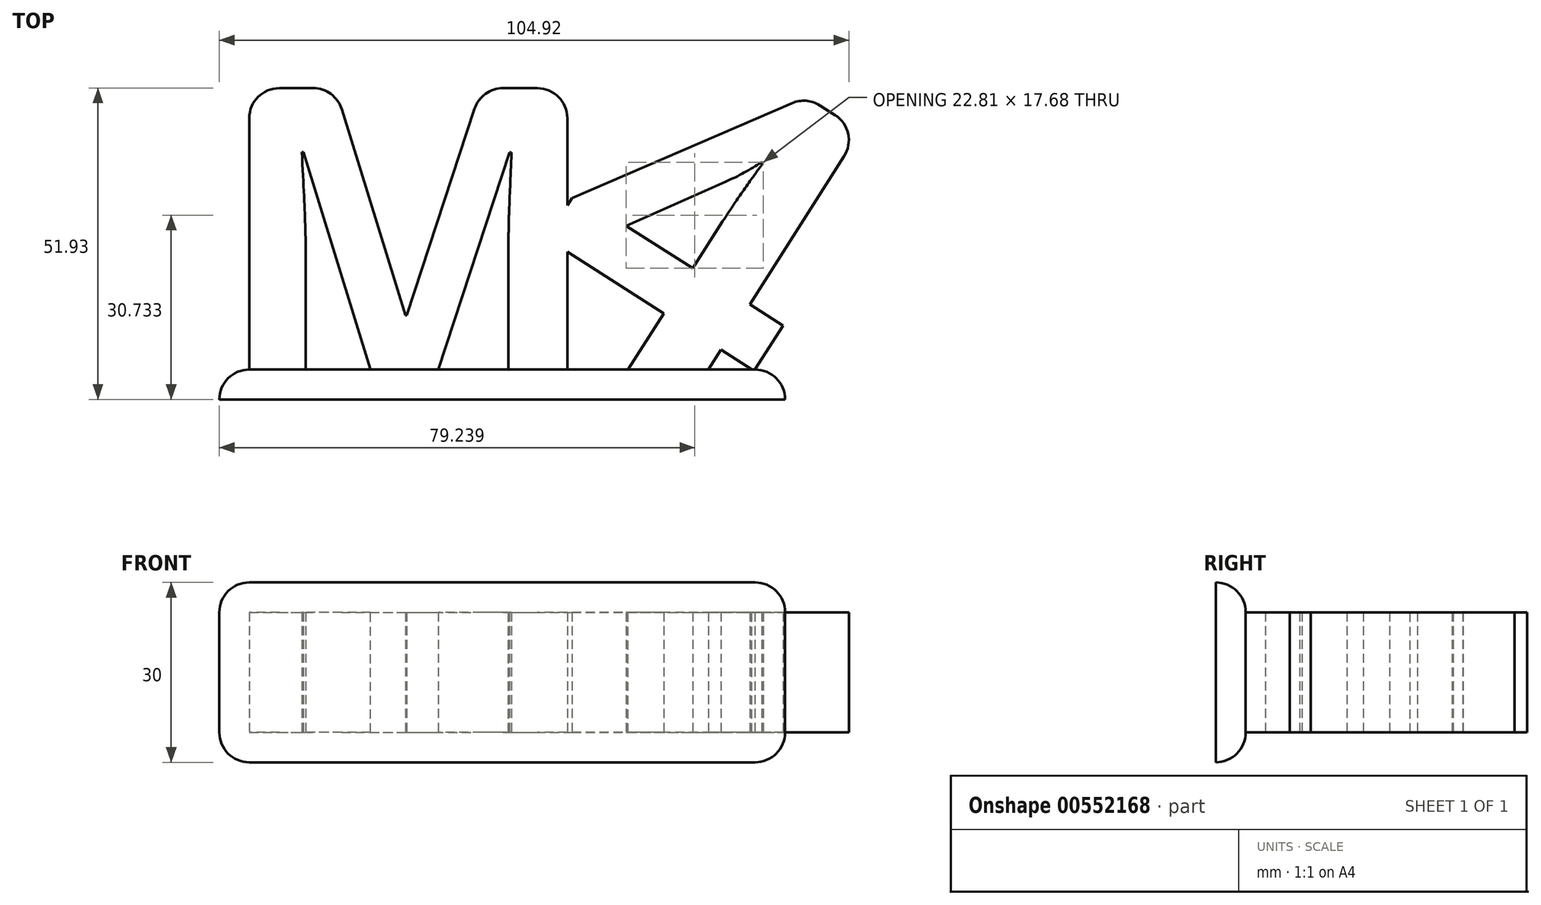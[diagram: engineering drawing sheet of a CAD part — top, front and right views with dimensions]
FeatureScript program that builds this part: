
annotation { "Feature Type Name" : "Feature", "Feature Type Description" : "" }
export const myFeature = defineFeature(function(context is Context, id is Id, definition is map)
    precondition{}
    {
        {
            var Q0;
            Q0=qCreatedBy(makeId("Top.planeOp"),FACE);
            var sketch = newSketch(context, id + "F0", { "sketchPlane" : qUnion([Q0])});
            skText(sketch, "E0", { "text": "M", "fontName": "OpenSans-Bold.ttf"});
            const initialGuessF0  = {"E0": [-0.04888, -0.02717, 1, 0, 0.05]};
            skSetInitialGuess(sketch, initialGuessF0);
            skSolve(sketch);
        }
        {
            var Q0;
            Q0=makeQuery(id+"F0.imprint","IMPRINT",FACE,{"disambiguationData":[TD([[makeQuery(id+"F0.imprint","IMPRINT",EDGE,{"derivedFrom":sQuery(id+"F0.wireOp",EDGE,"E0.sketch_text.stroke-0")}),-1.0]])]});
            extrude(context, id + "F1", {"entities" : qUnion([Q0]), "depth" : 20 * mm, "offsetDistance" : 25.4 * mm});
        }
        {
            var Q0;
            Q0=qCreatedBy(makeId("Top.planeOp"),FACE);
            var sketch = newSketch(context, id + "F2", { "sketchPlane" : qUnion([Q0])});
            skText(sketch, "E1", { "text": "4", "fontName": "OpenSans-Bold.ttf"});
            const initialGuessF2  = {"E1": [-0.00034, -0.01151, 0.8435, -0.53714, 0.055]};
            skSetInitialGuess(sketch, initialGuessF2);
            skSolve(sketch);
        }
        {
            var Q0;
            Q0=makeQuery(id+"F2.imprint","IMPRINT",FACE,{"disambiguationData":[TD([[makeQuery(id+"F2.imprint","IMPRINT",EDGE,{"derivedFrom":sQuery(id+"F2.wireOp",EDGE,"E1.sketch_text.stroke-0")}),-1.0]])]});
            var sketch = newSketch(context, id + "F3", { "sketchPlane" : qUnion([Q0])});
            skLineSegment(sketch, "E2", {"start": v(-47.64, -24.52) * mm, "end": v(-47.64, -29.52) * mm});
            skLineSegment(sketch, "E3", {"start": v(46.66, -24.52) * mm, "end": v(46.66, -29.52) * mm});
            skLineSegment(sketch, "E4", {"start": v(46.66, -29.52) * mm, "end": v(-47.64, -29.52) * mm});
            skLineSegment(sketch, "E5", {"start": v(46.66, -24.52) * mm, "end": v(-47.64, -24.52) * mm});
            skSolve(sketch);
        }
        {
            var Q0;
            Q0=makeQuery(id+"F2.imprint","IMPRINT",FACE,{"disambiguationData":[TD([[makeQuery(id+"F2.imprint","IMPRINT",EDGE,{"derivedFrom":sQuery(id+"F2.wireOp",EDGE,"E1.sketch_text.stroke-0")}),-1.0]])]});
            extrude(context, id + "F4", {"entities" : qUnion([Q0]), "operationType" : NewBodyOperationType.ADD, "depth" : 20 * mm, "offsetDistance" : 25 * mm});
        }
        {
            var Q0;
            Q0=makeQuery(id+"F1.opExtrude","SWEPT_EDGE",EDGE,{"disambiguationData":[OSD([sQuery(id+"F0.wireOp",EDGE,"E0.sketch_text.stroke-5"),sQuery(id+"F0.wireOp",EDGE,"E0.sketch_text.stroke-6")])]});
            fillet(context, id + "F5", {"entities" : qUnion([Q0]), "radius" : 5 * mm, "tangentPropagation" : true, "allowEdgeOverflow" : false});
        }
        {
            var Q0;
            Q0=makeQuery(id+"F1.opExtrude","SWEPT_EDGE",EDGE,{"disambiguationData":[OSD([sQuery(id+"F0.wireOp",EDGE,"E0.sketch_text.stroke-6"),sQuery(id+"F0.wireOp",EDGE,"E0.sketch_text.stroke-7")])]});
            fillet(context, id + "F6", {"entities" : qUnion([Q0]), "radius" : 5 * mm, "tangentPropagation" : true, "allowEdgeOverflow" : false});
        }
        {
            var Q0;
            Q0=makeQuery(id+"F1.opExtrude","SWEPT_EDGE",EDGE,{"disambiguationData":[OSD([sQuery(id+"F0.wireOp",EDGE,"E0.sketch_text.stroke-9"),sQuery(id+"F0.wireOp",EDGE,"E0.sketch_text.stroke-10")])]});
            fillet(context, id + "F7", {"entities" : qUnion([Q0]), "radius" : 5 * mm, "tangentPropagation" : true, "allowEdgeOverflow" : false});
        }
        {
            var Q0;
            Q0=makeQuery(id+"F1.opExtrude","SWEPT_EDGE",EDGE,{"disambiguationData":[OSD([sQuery(id+"F0.wireOp",EDGE,"E0.sketch_text.stroke-10"),sQuery(id+"F0.wireOp",EDGE,"E0.sketch_text.stroke-11")])]});
            fillet(context, id + "F8", {"entities" : qUnion([Q0]), "radius" : 5 * mm, "tangentPropagation" : true, "allowEdgeOverflow" : false});
        }
        {
            var Q0;
            {var subQ6=sQuery(id+"F3.wireOp",EDGE,"E2");Q0=makeQuery(id+"F3.imprint","IMPRINT",FACE,{"disambiguationData":[TD([[makeQuery(id+"F3.imprint","IMPRINT",EDGE,{"derivedFrom":subQ6}),1.0]])]});}
            var Q1;
            {var subQ3=sQuery(id+"F3.wireOp",EDGE,"E4");var subQ5=makeQuery(id+"F2.imprint","IMPRINT",EDGE,{"derivedFrom":sQuery(id+"F2.wireOp",EDGE,"E1.sketch_text.stroke-1")});var subQ6=makeQuery(id+"F3.imprint","INTERSECT",VERTEX,{"derivedFrom":[subQ5,subQ3]});Q1=makeQuery(id+"F3.imprint","IMPRINT",FACE,{"disambiguationData":[TD([[makeQuery(id+"F3.imprint","IMPRINT",EDGE,{"disambiguationData":[TD([[subQ6,-1.0]])],"derivedFrom":subQ3}),-1.0]])]});}
            var Q2;
            {var subQ1=sQuery(id+"F3.wireOp",EDGE,"E3");Q2=makeQuery(id+"F3.imprint","IMPRINT",FACE,{"disambiguationData":[TD([[makeQuery(id+"F3.imprint","IMPRINT",EDGE,{"derivedFrom":subQ1}),-1.0]])]});}
            var Q3;
            {var subQ0=sQuery(id+"F3.wireOp",EDGE,"E5");var subQ1=makeQuery(id+"F2.imprint","IMPRINT",EDGE,{"derivedFrom":sQuery(id+"F2.wireOp",EDGE,"E1.sketch_text.stroke-10")});var subQ2=makeQuery(id+"F3.imprint","INTERSECT",VERTEX,{"derivedFrom":[subQ1,subQ0]});Q3=makeQuery(id+"F3.imprint","IMPRINT",FACE,{"disambiguationData":[TD([[makeQuery(id+"F3.imprint","IMPRINT",EDGE,{"disambiguationData":[TD([[subQ2,-1.0]])],"derivedFrom":subQ0}),1.0]])]});}
            extrude(context, id + "F9", {"entities" : qUnion([Q0, Q1, Q2, Q3]), "operationType" : NewBodyOperationType.ADD, "depth" : 25 * mm, "offsetDistance" : 25 * mm, "hasSecondDirection" : true, "secondDirectionOppositeDirection" : true, "secondDirectionDepth" : 5 * mm});
        }
        {
            var Q0;
            {var subQ0=sQuery(id+"F3.wireOp",EDGE,"E4");var subQ1=makeQuery(id+"F2.imprint","IMPRINT",EDGE,{"derivedFrom":sQuery(id+"F2.wireOp",EDGE,"E1.sketch_text.stroke-1")});var subQ2=makeQuery(id+"F3.imprint","INTERSECT",VERTEX,{"derivedFrom":[subQ1,subQ0]});Q0=makeQuery(id+"F3.imprint","IMPRINT",FACE,{"disambiguationData":[TD([[makeQuery(id+"F3.imprint","IMPRINT",EDGE,{"disambiguationData":[TD([[subQ2,-1.0]])],"derivedFrom":subQ0}),1.0]])]});}
            extrude(context, id + "F10", {"entities" : qUnion([Q0]), "operationType" : NewBodyOperationType.REMOVE, "endBound" : BoundingType.SYMMETRIC, "oppositeDirection" : true, "depth" : 60 * mm, "offsetDistance" : 25 * mm});
        }
        {
            var Q0;
            Q0=makeQuery(id+"F9.opExtrude","SWEPT_EDGE",EDGE,{"disambiguationData":[OSD([sQuery(id+"F3.wireOp",EDGE,"E2"),sQuery(id+"F3.wireOp",EDGE,"E5")])]});
            fillet(context, id + "F11", {"entities" : qUnion([Q0]), "radius" : 5 * mm, "tangentPropagation" : true, "allowEdgeOverflow" : false});
        }
        {
            var Q0;
            Q0=makeQuery(id+"F9.opExtrude","SWEPT_EDGE",EDGE,{"disambiguationData":[OSD([sQuery(id+"F3.wireOp",EDGE,"E3"),sQuery(id+"F3.wireOp",EDGE,"E5")])]});
            fillet(context, id + "F12", {"entities" : qUnion([Q0]), "radius" : 5 * mm, "tangentPropagation" : true, "allowEdgeOverflow" : false});
        }
        {
            var Q0;
            Q0=makeQuery(id+"F9.opExtrude","CAP_EDGE",EDGE,{"disambiguationData":[OSD([sQuery(id+"F3.wireOp",EDGE,"E5")])],"isStart":false});
            var Q1;
            Q1=makeQuery(id+"F9.opExtrude","CAP_EDGE",EDGE,{"disambiguationData":[OSD([sQuery(id+"F3.wireOp",EDGE,"E5")])],"isStart":true});
            fillet(context, id + "F13", {"entities" : qUnion([Q0, Q1]), "radius" : 5 * mm, "tangentPropagation" : true, "allowEdgeOverflow" : false});
        }
        {
            var Q0;
            Q0=makeQuery(id+"F4.opExtrude","SWEPT_EDGE",EDGE,{"disambiguationData":[OSD([sQuery(id+"F2.wireOp",EDGE,"E1.sketch_text.stroke-6"),sQuery(id+"F2.wireOp",EDGE,"E1.sketch_text.stroke-7")])]});
            fillet(context, id + "F14", {"entities" : qUnion([Q0]), "radius" : 5 * mm, "tangentPropagation" : true, "allowEdgeOverflow" : false});
        }
        {
            var Q0;
            Q0=makeQuery(id+"F4.opExtrude","SWEPT_EDGE",EDGE,{"disambiguationData":[OSD([sQuery(id+"F2.wireOp",EDGE,"E1.sketch_text.stroke-7"),sQuery(id+"F2.wireOp",EDGE,"E1.sketch_text.stroke-8")])]});
            fillet(context, id + "F15", {"entities" : qUnion([Q0]), "radius" : 5 * mm, "tangentPropagation" : true, "allowEdgeOverflow" : false});
        }
    });
